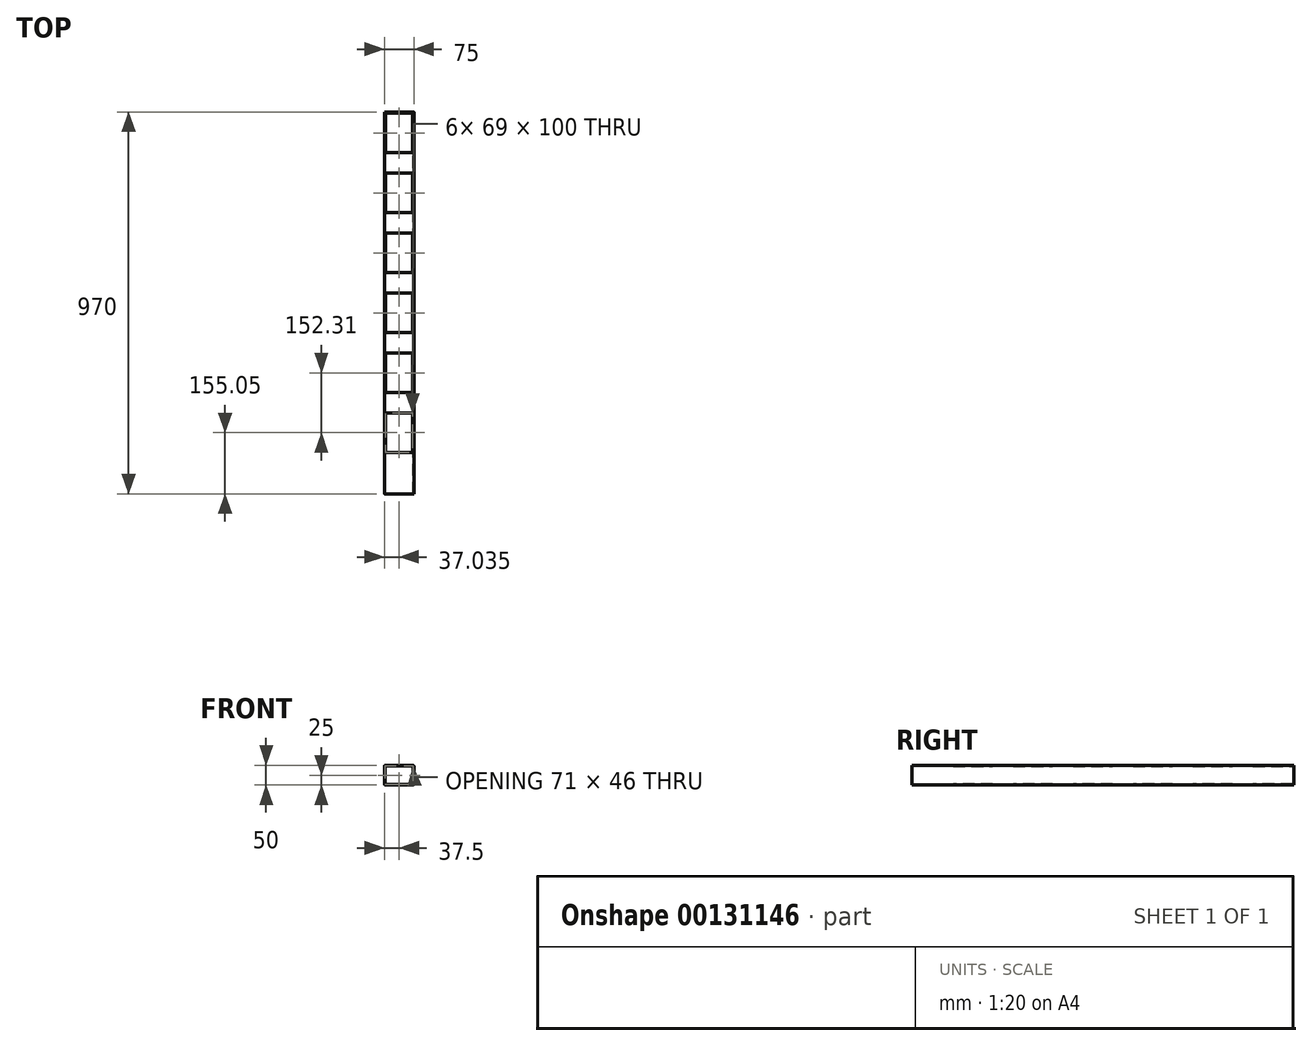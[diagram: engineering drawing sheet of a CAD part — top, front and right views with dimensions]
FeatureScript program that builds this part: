
annotation { "Feature Type Name" : "Feature", "Feature Type Description" : "" }
export const myFeature = defineFeature(function(context is Context, id is Id, definition is map)
    precondition{}
    {
        {
            var Q0;
            Q0=qCreatedBy(makeId("Front.planeOp"),FACE);
            var sketch = newSketch(context, id + "F0", { "sketchPlane" : qUnion([Q0])});
            skLineSegment(sketch, "E0.bottom", {"start": v(37.5, -25) * mm, "end": v(-37.5, -25) * mm});
            skLineSegment(sketch, "E0.top", {"start": v(37.5, 25) * mm, "end": v(-37.5, 25) * mm});
            skLineSegment(sketch, "E0.left", {"start": v(37.5, -25) * mm, "end": v(37.5, 25) * mm});
            skLineSegment(sketch, "E0.right", {"start": v(-37.5, -25) * mm, "end": v(-37.5, 25) * mm});
            skPoint(sketch, "E0.middle", {"position": v(0, 0) * mm});
            skLineSegment(sketch, "E1.bottom", {"start": v(35.5, -23) * mm, "end": v(-35.5, -23) * mm});
            skLineSegment(sketch, "E1.top", {"start": v(35.5, 23) * mm, "end": v(-35.5, 23) * mm});
            skLineSegment(sketch, "E1.left", {"start": v(35.5, -23) * mm, "end": v(35.5, 23) * mm});
            skLineSegment(sketch, "E1.right", {"start": v(-35.5, -23) * mm, "end": v(-35.5, 23) * mm});
            skSolve(sketch);
        }
        {
            var Q0;
            Q0=makeQuery(id+"F0.imprint","IMPRINT",FACE,{"disambiguationData":[TD([[makeQuery(id+"F0.imprint","IMPRINT",EDGE,{"derivedFrom":sQuery(id+"F0.wireOp",EDGE,"E0.bottom")}),-1.0]])]});
            extrude(context, id + "F1", {"entities" : qUnion([Q0]), "depth" : 970 * mm});
        }
        {
            var Q0;
            Q0=makeQuery(id+"F1.opExtrude","SWEPT_FACE",FACE,{"disambiguationData":[OSD([sQuery(id+"F0.wireOp",EDGE,"E0.top")])]});
            var sketch = newSketch(context, id + "F2", { "sketchPlane" : qUnion([Q0])});
            skLineSegment(sketch, "E2.bottom", {"start": v(34.03, -864.95) * mm, "end": v(-34.97, -864.95) * mm});
            skLineSegment(sketch, "E2.top", {"start": v(34.03, -764.95) * mm, "end": v(-34.97, -764.95) * mm});
            skLineSegment(sketch, "E2.left", {"start": v(34.03, -864.95) * mm, "end": v(34.03, -764.95) * mm});
            skLineSegment(sketch, "E2.right", {"start": v(-34.97, -864.95) * mm, "end": v(-34.97, -764.95) * mm});
            skPoint(sketch, "E2.middle", {"position": v(0, -485) * mm});
            skPoint(sketch, "E2.middle.positionSnap0", {"position": v(-37.5, -485) * mm});
            skPoint(sketch, "E2.centerSnap0", {"position": v(-37.5, -485) * mm});
            skLineSegment(sketch, "E3.bottom", {"start": v(34.03, -712.64) * mm, "end": v(-34.97, -712.64) * mm});
            skLineSegment(sketch, "E3.top", {"start": v(34.03, -612.64) * mm, "end": v(-34.97, -612.64) * mm});
            skLineSegment(sketch, "E3.left", {"start": v(34.03, -712.64) * mm, "end": v(34.03, -612.64) * mm});
            skLineSegment(sketch, "E3.right", {"start": v(-34.97, -712.64) * mm, "end": v(-34.97, -612.64) * mm});
            skLineSegment(sketch, "E4.bottom", {"start": v(34.03, -560.33) * mm, "end": v(-34.97, -560.33) * mm});
            skLineSegment(sketch, "E4.top", {"start": v(34.03, -460.33) * mm, "end": v(-34.97, -460.33) * mm});
            skLineSegment(sketch, "E4.left", {"start": v(34.03, -560.33) * mm, "end": v(34.03, -460.33) * mm});
            skLineSegment(sketch, "E4.right", {"start": v(-34.97, -560.33) * mm, "end": v(-34.97, -460.33) * mm});
            skLineSegment(sketch, "E5.bottom", {"start": v(34.03, -408.02) * mm, "end": v(-34.97, -408.02) * mm});
            skLineSegment(sketch, "E5.top", {"start": v(34.03, -308.02) * mm, "end": v(-34.97, -308.02) * mm});
            skLineSegment(sketch, "E5.left", {"start": v(34.03, -408.02) * mm, "end": v(34.03, -308.02) * mm});
            skLineSegment(sketch, "E5.right", {"start": v(-34.97, -408.02) * mm, "end": v(-34.97, -308.02) * mm});
            skPoint(sketch, "E5.middle", {"position": v(0.05, -26.06) * mm});
            skPoint(sketch, "E5.middle.positionSnap0", {"position": v(-37.45, -26.06) * mm});
            skPoint(sketch, "E5.centerSnap0", {"position": v(-37.45, -26.06) * mm});
            skLineSegment(sketch, "E6.bottom", {"start": v(34.03, -255.71) * mm, "end": v(-34.97, -255.71) * mm});
            skLineSegment(sketch, "E6.top", {"start": v(34.03, -155.71) * mm, "end": v(-34.97, -155.71) * mm});
            skLineSegment(sketch, "E6.left", {"start": v(34.03, -255.71) * mm, "end": v(34.03, -155.71) * mm});
            skLineSegment(sketch, "E6.right", {"start": v(-34.97, -255.71) * mm, "end": v(-34.97, -155.71) * mm});
            skLineSegment(sketch, "E7.bottom", {"start": v(34.03, -103.4) * mm, "end": v(-34.97, -103.4) * mm});
            skLineSegment(sketch, "E7.top", {"start": v(34.03, -3.4) * mm, "end": v(-34.97, -3.4) * mm});
            skLineSegment(sketch, "E7.left", {"start": v(34.03, -103.4) * mm, "end": v(34.03, -3.4) * mm});
            skLineSegment(sketch, "E7.right", {"start": v(-34.97, -103.4) * mm, "end": v(-34.97, -3.4) * mm});
            skSolve(sketch);
        }
        {
            var Q0;
            Q0=makeQuery(id+"F1.opExtrude","SWEPT_EDGE",EDGE,{"disambiguationData":[OSD([sQuery(id+"F0.wireOp",EDGE,"E0.top"),sQuery(id+"F0.wireOp",EDGE,"E0.right")])]});
            var Q1;
            Q1=makeQuery(id+"F1.opExtrude","SWEPT_EDGE",EDGE,{"disambiguationData":[OSD([sQuery(id+"F0.wireOp",EDGE,"E0.top"),sQuery(id+"F0.wireOp",EDGE,"E0.left")])]});
            var Q2;
            Q2=makeQuery(id+"F1.opExtrude","SWEPT_EDGE",EDGE,{"disambiguationData":[OSD([sQuery(id+"F0.wireOp",EDGE,"E0.bottom"),sQuery(id+"F0.wireOp",EDGE,"E0.left")])]});
            var Q3;
            Q3=makeQuery(id+"F1.opExtrude","SWEPT_EDGE",EDGE,{"disambiguationData":[OSD([sQuery(id+"F0.wireOp",EDGE,"E0.bottom"),sQuery(id+"F0.wireOp",EDGE,"E0.right")])]});
            fillet(context, id + "F3", {"entities" : qUnion([Q0, Q1, Q2, Q3]), "radius" : 2 * mm, "tangentPropagation" : true, "allowEdgeOverflow" : false});
        }
        {
            var Q0;
            Q0=makeQuery(id+"F1.opExtrude","SWEPT_EDGE",EDGE,{"disambiguationData":[OSD([sQuery(id+"F0.wireOp",EDGE,"E1.top"),sQuery(id+"F0.wireOp",EDGE,"E1.right")])]});
            var Q1;
            Q1=makeQuery(id+"F1.opExtrude","SWEPT_EDGE",EDGE,{"disambiguationData":[OSD([sQuery(id+"F0.wireOp",EDGE,"E1.bottom"),sQuery(id+"F0.wireOp",EDGE,"E1.right")])]});
            var Q2;
            Q2=makeQuery(id+"F1.opExtrude","SWEPT_EDGE",EDGE,{"disambiguationData":[OSD([sQuery(id+"F0.wireOp",EDGE,"E1.bottom"),sQuery(id+"F0.wireOp",EDGE,"E1.left")])]});
            var Q3;
            Q3=makeQuery(id+"F1.opExtrude","SWEPT_EDGE",EDGE,{"disambiguationData":[OSD([sQuery(id+"F0.wireOp",EDGE,"E1.top"),sQuery(id+"F0.wireOp",EDGE,"E1.left")])]});
            fillet(context, id + "F4", {"entities" : qUnion([Q0, Q1, Q2, Q3]), "radius" : 2 * mm, "tangentPropagation" : true, "allowEdgeOverflow" : false});
        }
        {
            var Q0;
            Q0=qSketchRegion(id+"F2",true);
            extrude(context, id + "F5", {"entities" : qUnion([Q0]), "operationType" : NewBodyOperationType.REMOVE, "oppositeDirection" : true, "depth" : 60 * mm});
        }
    });
